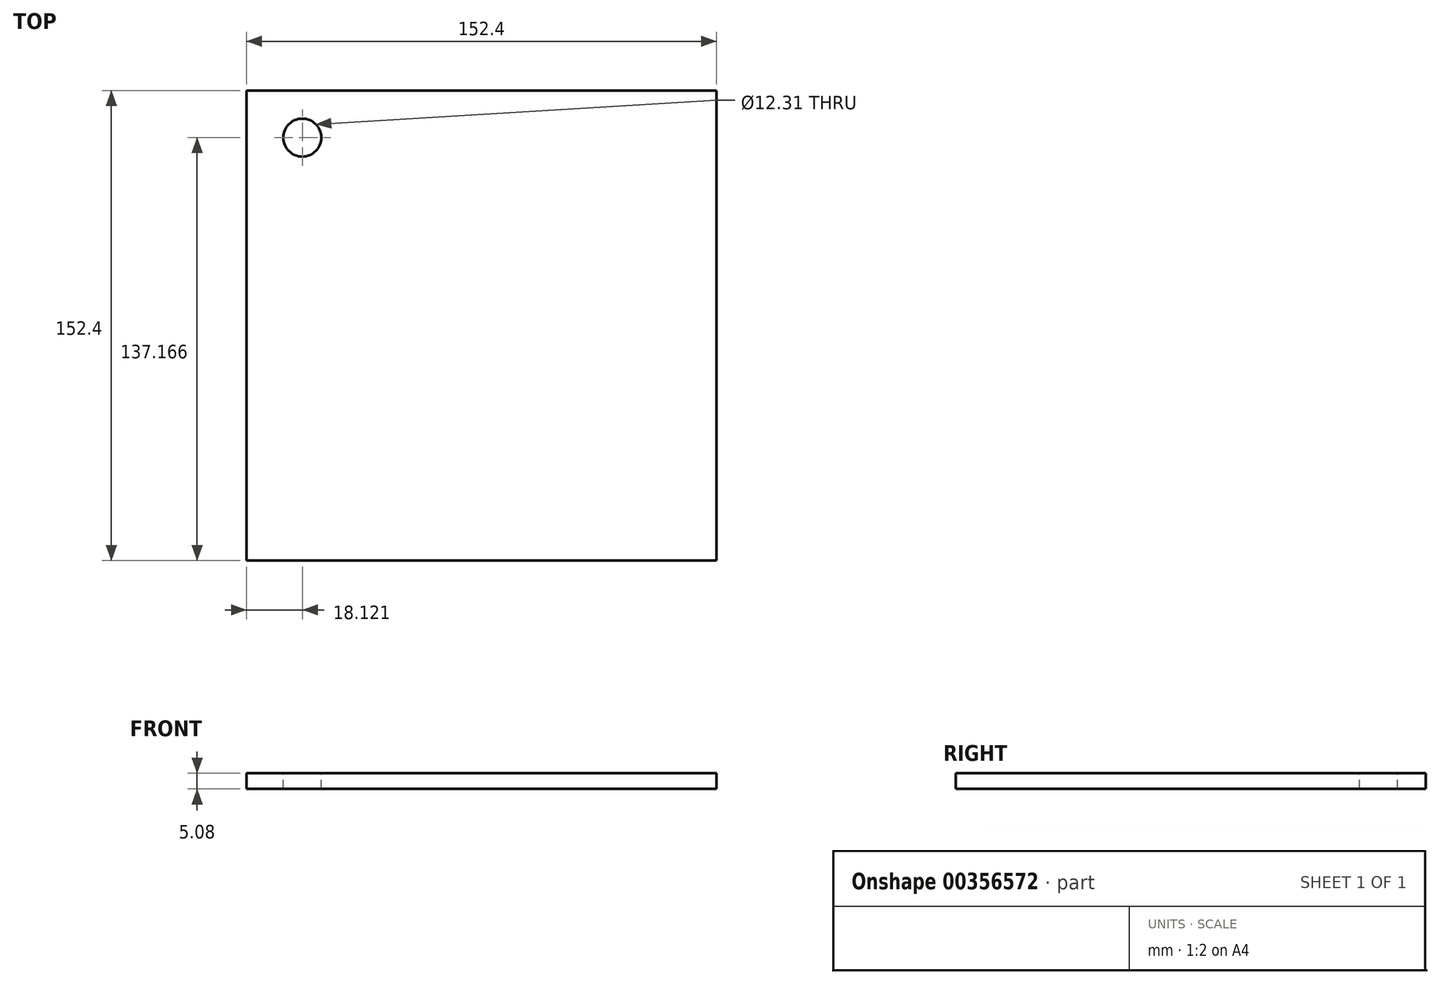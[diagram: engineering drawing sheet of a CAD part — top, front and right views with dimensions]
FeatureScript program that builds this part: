
annotation { "Feature Type Name" : "Feature", "Feature Type Description" : "" }
export const myFeature = defineFeature(function(context is Context, id is Id, definition is map)
    precondition{}
    {
        {
            var Q0;
            Q0=qCreatedBy(makeId("Top.planeOp"),FACE);
            var sketch = newSketch(context, id + "F0", { "sketchPlane" : qUnion([Q0])});
            skLineSegment(sketch, "E0.bottom", {"start": v(76.2, -76.2) * mm, "end": v(-76.2, -76.2) * mm});
            skLineSegment(sketch, "E0.top", {"start": v(76.2, 76.2) * mm, "end": v(-76.2, 76.2) * mm});
            skLineSegment(sketch, "E0.left", {"start": v(76.2, -76.2) * mm, "end": v(76.2, 76.2) * mm});
            skLineSegment(sketch, "E0.right", {"start": v(-76.2, -76.2) * mm, "end": v(-76.2, 76.2) * mm});
            skPoint(sketch, "E0.middle", {"position": v(0, 0) * mm});
            skSolve(sketch);
        }
        {
            var Q0;
            Q0 = qSketchRegion(id + "F0", true);
            extrude(context, id + "F1", {"entities" : qUnion([Q0]), "depth" : 5.08 * mm, "offsetDistance" : 25.4 * mm});
        }
        {
            var Q0;
            Q0=makeQuery(id+"F1.opExtrude","CAP_FACE",FACE,{"disambiguationData":[OSD([sQuery(id+"F0.wireOp",EDGE,"E0.bottom"),sQuery(id+"F0.wireOp",EDGE,"E0.top"),sQuery(id+"F0.wireOp",EDGE,"E0.left"),sQuery(id+"F0.wireOp",EDGE,"E0.right")])],"isStart":false});
            var sketch = newSketch(context, id + "F2", { "sketchPlane" : qUnion([Q0])});
            skCircle(sketch, "E1", {"center": v(-58.08, 60.97) * mm, "radius": 6.16 * mm});
            skSolve(sketch);
        }
        {
            var Q0;
            Q0=makeQuery(id+"F2.imprint","IMPRINT",FACE,{"disambiguationData":[TD([[makeQuery(id+"F2.imprint","IMPRINT",EDGE,{"derivedFrom":sQuery(id+"F2.wireOp",EDGE,"E1")}),1.0]])]});
            extrude(context, id + "F3", {"entities" : qUnion([Q0]), "operationType" : NewBodyOperationType.REMOVE, "oppositeDirection" : true, "depth" : 25.4 * mm, "offsetDistance" : 25.4 * mm});
        }
    });
